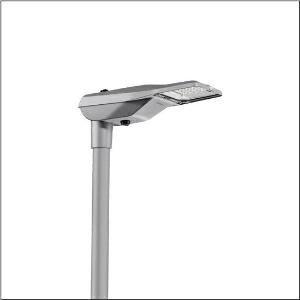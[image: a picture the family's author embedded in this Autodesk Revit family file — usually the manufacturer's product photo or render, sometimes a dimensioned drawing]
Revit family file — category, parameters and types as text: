
# Revit family: streetlight_sl_21_iq_micro___st1_0a_5xe1d21y08db_e1fc
name_source: partatom
category: Lighting Fixtures
units: mm (PartAtom-declared; Revit-internal decimal feet)

## family parameters
Cut with Voids When Loaded = No
Host = Face
Light Source = No
Part Type = Normal
Room Calculation Point = No
Round Connector Dimension = Use Diameter
Shared = No

## types (1)
- --- (1 x LED, 4100 lm, 39.1 W, 2200K)
    Apparent Load = 39 VA
    CIE Flux Codes = 37 72 97 100 100
    Color Rendering = 70
    Color Temperature = 2200K
    Default Elevation = 1800 mm
    Description = Streetlight SL 21 iQ micro, mast luminaire, primary light control with lens, of PMMA, primary optical cover: cover, of toughened safety glass, transparent, light distribution: ST1.0a, light emission: direct distribution, primary light characteristic: asymmetric, installation type: post-top, side-entry, LED, High Power LED, rated luminous flux: 4.100lm, luminous efficacy: 105lm/W, light colour: 722, colour temperature: 2200K, control: presetting dimming logarithmic, Street-Remote, Auto-Match, Temp-Guard, Lumen-Switch, Night-Set, Smart-Wire, Light-Fading, Desk-Remote (wireless, voltage-free reading and setting of iQ features in the workshop via application-optimized NFC function/RFID function), optimised constant luminous flux control (CLO 2.0), mains connection: 220..240V, AC, 50/60Hz, start of lifetime: 39W, end of service life: 41W, reduction: 17W, luminaire housing, of diecast aluminium, powder-coated, Siteco® metallic grey (DB 702S), corrosivity category C5 mid according to DIN EN ISO 12944, please order mast flange separately, inclination adjustable: 0°, 5°, 10°, 15°, sealing non-destructively replaceable, multi-level sealing system, length: 528mm, width: 235mm, height: 110mm, mast flange for spigot size: 42mm (side-entry): 5XC10008XM4, 60/48mm (side-entry/post-top): 5XC10108XM2, 76/60mm (side-entry/post-top): 5XC10108XM1, Smart Interface below and above, protection rating (complete): IP66, insulation class (complete): insulation class II (safety insulation), certification: CE, ENEC, ENEC+, VDE, impact resistance: IK09, permissible operating ambient temperature for outdoor applications: -40..+50°C, standard-compliant lighting for roads and squares, packaging unit: 1 piece

Light Distribution: ST1.0a
    Height = 110 mm
    Lamp = 1 x LED
    Lamp Light Flux = 4100 lm
    Lamp Power = 39.1 W
    Lamp count = 1
    Length = 528 mm
    Luminous efficacy = 105 lm/W
    Manufacturer = Siteco
    ModVariant = No
    Model = 5XE1D21Y08DB
    Number of Poles = 1
    OnlyDefault = Yes
    Power Factor = 1
    Product Name = Streetlight SL 21 iQ micro | ST1.0a
    Product group = mast luminaire | pylon top
    ProductGroupID = 6100
    Protection Class = Protection class II
    Protection Degree = IP 66
    RLX_Detail_Level = 1
    RLX_Emergency_Light_Flux = 0 lm
    RLX_Emergency_Type = 0
    RLX_Emergency_Type_DB = No
    RlxData = <blob elided: 98417 chars, md5=6380607c>
    Socket = socket
    Standby Power = 0 W
    System Light Flux = 4100 lm
    System Power = 39 W
    Type Comments = factory setting: luminous flux: 100 % | dim-lin: 254 | 765 mA
    Type Image = l_1007239.jpg
    URL = http://relux.com
    VarID = @adj_045609
    Voltage = 0 V
    Weight = 0.00 kg
    Width = 235 mm

## geometry (parser evidence)
native form markers: Blend x4, Sweep x11
no freeform markers — native parametric forms only
